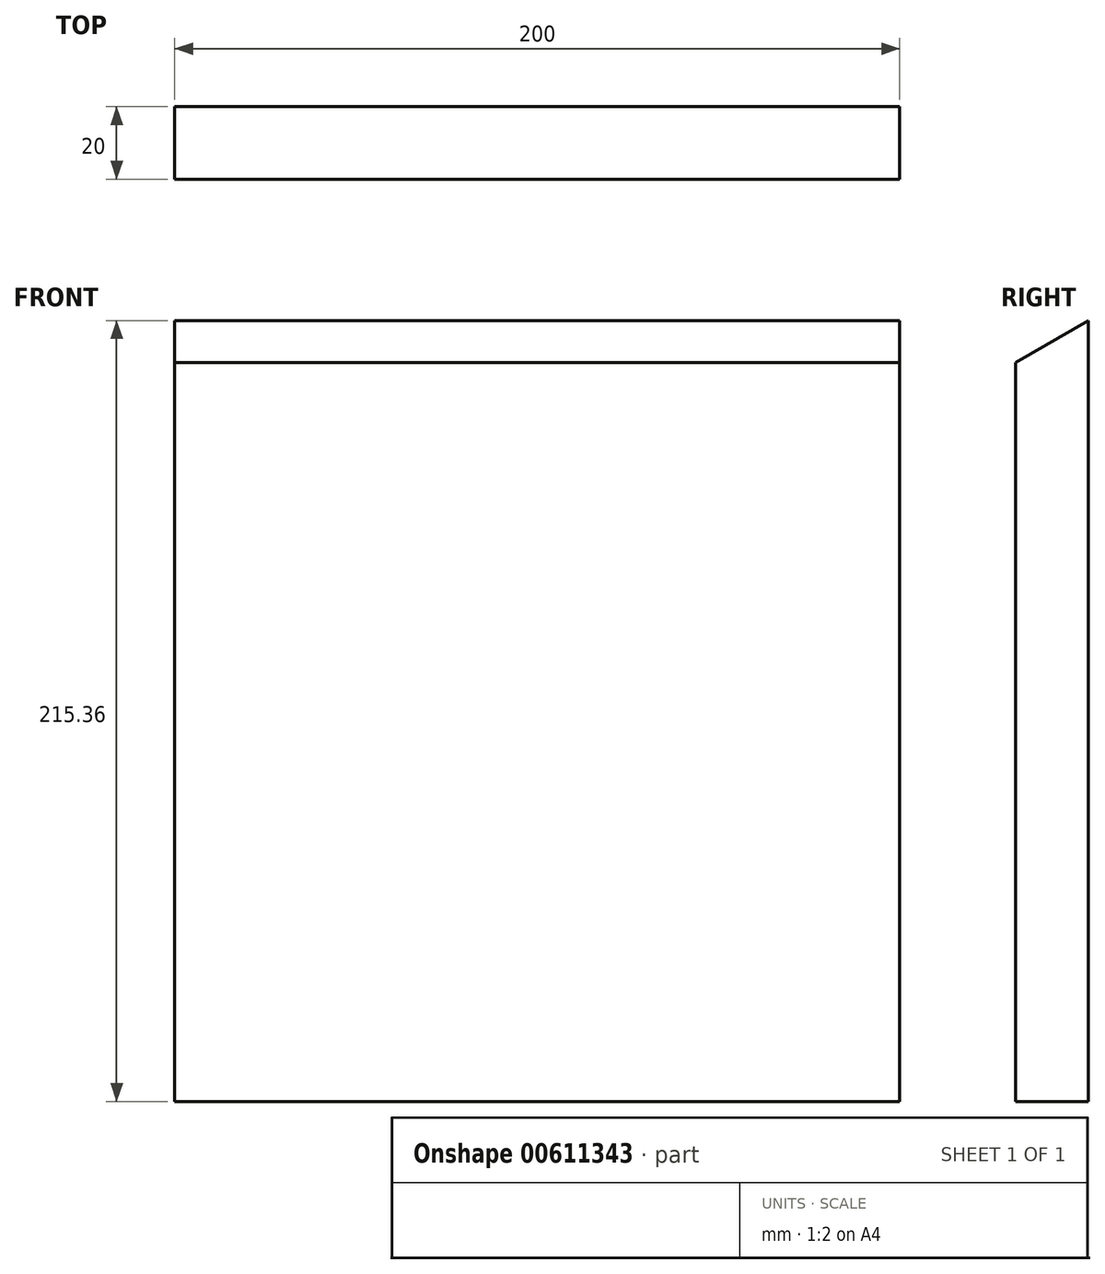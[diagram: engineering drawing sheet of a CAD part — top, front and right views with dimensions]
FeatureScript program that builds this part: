
annotation { "Feature Type Name" : "Feature", "Feature Type Description" : "" }
export const myFeature = defineFeature(function(context is Context, id is Id, definition is map)
    precondition{}
    {
        {
            var Q0;
            Q0=qCreatedBy(makeId("Front.planeOp"),FACE);
            var sketch = newSketch(context, id + "F0", { "sketchPlane" : qUnion([Q0])});
            skLineSegment(sketch, "E0.bottom", {"start": v(100, 107.68) * mm, "end": v(-100, 107.68) * mm});
            skLineSegment(sketch, "E0.top", {"start": v(100, -107.68) * mm, "end": v(-100, -107.68) * mm});
            skLineSegment(sketch, "E0.left", {"start": v(100, 107.68) * mm, "end": v(100, -107.68) * mm});
            skLineSegment(sketch, "E0.right", {"start": v(-100, 107.68) * mm, "end": v(-100, -107.68) * mm});
            skPoint(sketch, "E0.middle", {"position": v(0, 0) * mm});
            skSolve(sketch);
        }
        {
            var Q0;
            Q0=makeQuery(id+"F0.imprint","IMPRINT",FACE,{"disambiguationData":[TD([[makeQuery(id+"F0.imprint","IMPRINT",EDGE,{"derivedFrom":sQuery(id+"F0.wireOp",EDGE,"E0.bottom")}),1.0]])]});
            extrude(context, id + "F1", {"entities" : qUnion([Q0]), "depth" : 20 * mm, "offsetDistance" : 25 * mm});
        }
        {
            var Q0;
            Q0=makeQuery(id+"F1.opExtrude","SWEPT_FACE",FACE,{"disambiguationData":[OSD([sQuery(id+"F0.wireOp",EDGE,"E0.right")])]});
            var sketch = newSketch(context, id + "F2", { "sketchPlane" : qUnion([Q0])});
            skLineSegment(sketch, "E1", {"start": v(0, 107.68) * mm, "end": v(20, 96.13) * mm});
            skLineSegment(sketch, "E2", {"start": v(20, 96.13) * mm, "end": v(20, 96.13) * mm});
            skLineSegment(sketch, "E3", {"start": v(20, 107.68) * mm, "end": v(20, 96.13) * mm});
            skLineSegment(sketch, "E4", {"start": v(20, 107.68) * mm, "end": v(0, 107.68) * mm});
            skSolve(sketch);
        }
        {
            var Q0;
            Q0=makeQuery(id+"F2.imprint","IMPRINT",FACE,{"disambiguationData":[TD([[makeQuery(id+"F2.imprint","IMPRINT",EDGE,{"derivedFrom":sQuery(id+"F2.wireOp",EDGE,"E1")}),1.0]])]});
            extrude(context, id + "F3", {"entities" : qUnion([Q0]), "operationType" : NewBodyOperationType.REMOVE, "endBound" : BoundingType.THROUGH_ALL, "oppositeDirection" : true, "depth" : 25 * mm, "offsetDistance" : 25 * mm});
        }
    });
